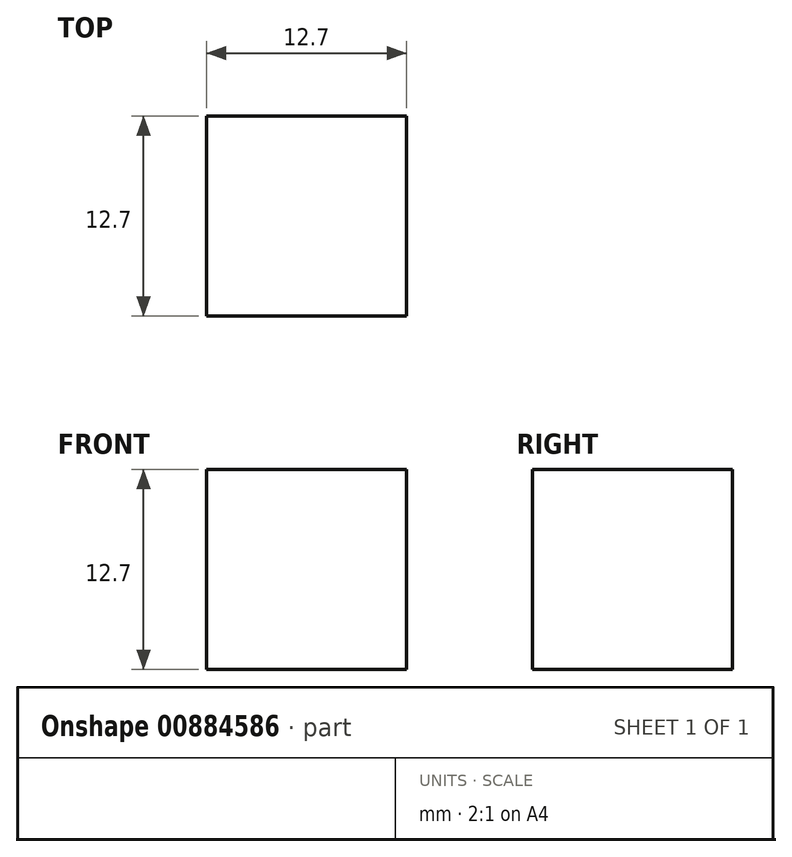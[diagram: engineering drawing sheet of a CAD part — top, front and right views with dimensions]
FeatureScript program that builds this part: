
annotation { "Feature Type Name" : "Feature", "Feature Type Description" : "" }
export const myFeature = defineFeature(function(context is Context, id is Id, definition is map)
    precondition{}
    {
        {
            var Q0;
            Q0=qCreatedBy(makeId("Top.planeOp"),FACE);
            var sketch = newSketch(context, id + "F0", { "sketchPlane" : qUnion([Q0])});
            skLineSegment(sketch, "E0.bottom", {"start": v(6.35, 6.35) * mm, "end": v(-6.35, 6.35) * mm});
            skLineSegment(sketch, "E0.top", {"start": v(6.35, -6.35) * mm, "end": v(-6.35, -6.35) * mm});
            skLineSegment(sketch, "E0.left", {"start": v(6.35, 6.35) * mm, "end": v(6.35, -6.35) * mm});
            skLineSegment(sketch, "E0.right", {"start": v(-6.35, 6.35) * mm, "end": v(-6.35, -6.35) * mm});
            skPoint(sketch, "E0.middle", {"position": v(0, 0) * mm});
            skSolve(sketch);
        }
        {
            var Q0;
            Q0=makeQuery(id+"F0.imprint","IMPRINT",FACE,{"disambiguationData":[TD([[makeQuery(id+"F0.imprint","IMPRINT",EDGE,{"derivedFrom":sQuery(id+"F0.wireOp",EDGE,"E0.bottom")}),1.0]])]});
            extrude(context, id + "F1", {"entities" : qUnion([Q0]), "depth" : 12.7 * mm, "offsetDistance" : 25.4 * mm});
        }
    });
